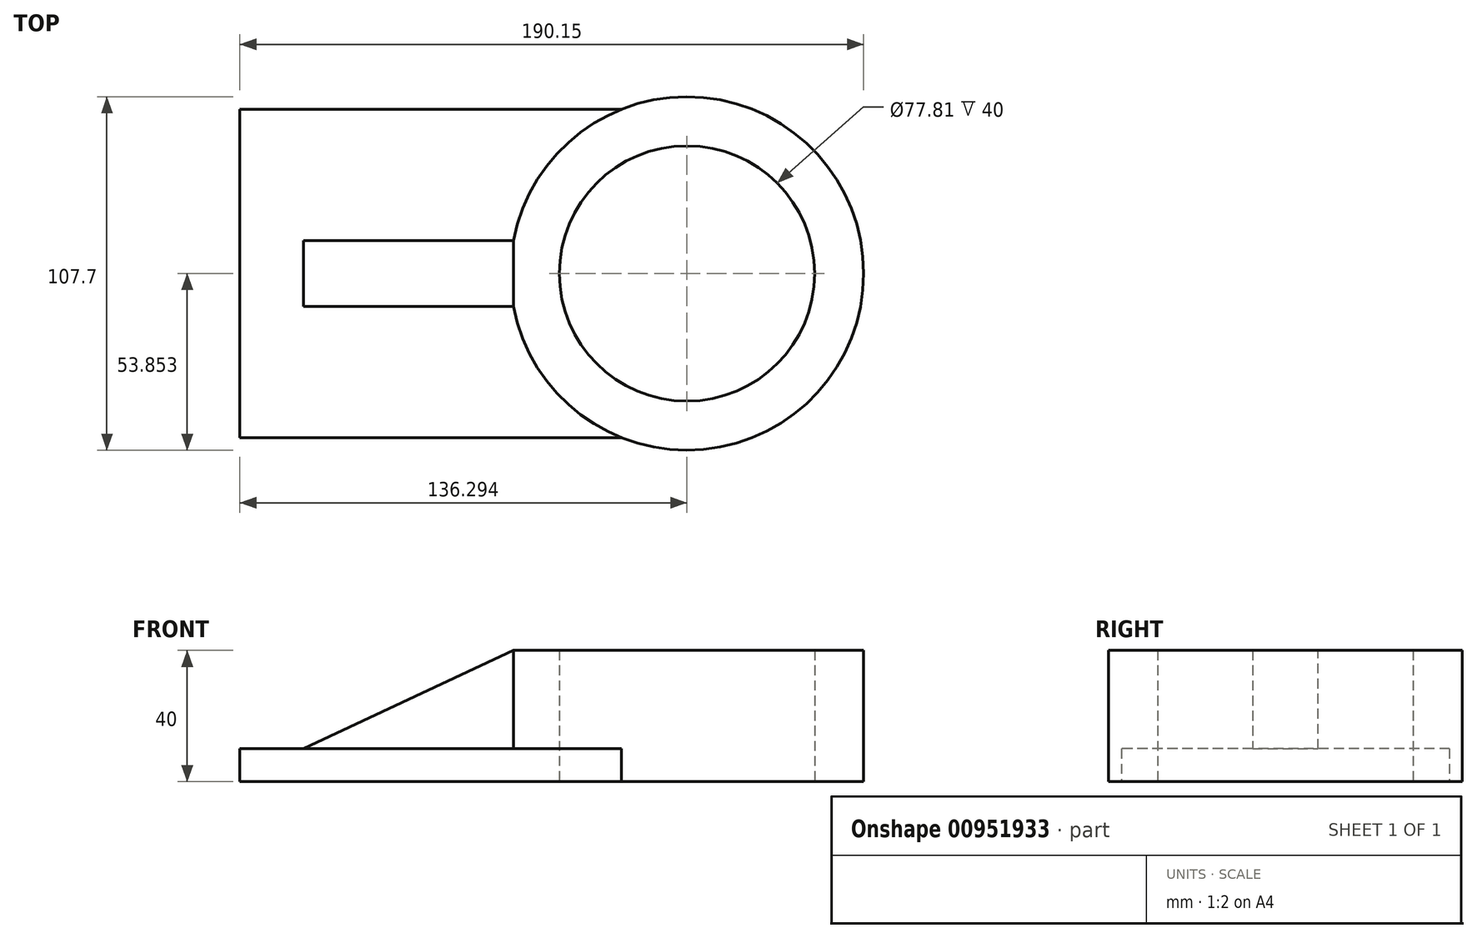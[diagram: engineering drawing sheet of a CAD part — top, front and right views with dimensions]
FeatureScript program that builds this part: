
annotation { "Feature Type Name" : "Feature", "Feature Type Description" : "" }
export const myFeature = defineFeature(function(context is Context, id is Id, definition is map)
    precondition{}
    {
        {
            var Q0;
            Q0=qCreatedBy(makeId("Top.planeOp"),FACE);
            var sketch = newSketch(context, id + "F0", { "sketchPlane" : qUnion([Q0])});
            skLineSegment(sketch, "E0.bottom", {"start": v(-44.41, 49.03) * mm, "end": v(71.88, 49.03) * mm});
            skLineSegment(sketch, "E0.top", {"start": v(-44.41, -50.97) * mm, "end": v(71.88, -50.97) * mm});
            skLineSegment(sketch, "E0.left", {"start": v(-44.41, 49.03) * mm, "end": v(-44.41, -50.97) * mm});
            skCircle(sketch, "E1", {"center": v(91.88, -0.97) * mm, "radius": 53.85 * mm});
            skCircle(sketch, "E2", {"center": v(91.88, -0.97) * mm, "radius": 38.9 * mm});
            skSolve(sketch);
        }
        {
            var Q0;
            Q0=makeQuery(id+"F0.imprint","IMPRINT",FACE,{"disambiguationData":[TD([[makeQuery(id+"F0.imprint","IMPRINT",EDGE,{"derivedFrom":sQuery(id+"F0.wireOp",EDGE,"E2")}),-1.0]])]});
            extrude(context, id + "F1", {"entities" : qUnion([Q0]), "depth" : 40 * mm, "offsetDistance" : 25 * mm});
        }
        {
            var Q0;
            {var subQ0=sQuery(id+"F0.wireOp",EDGE,"E0.bottom");Q0=makeQuery(id+"F0.imprint","IMPRINT",FACE,{"disambiguationData":[TD([[makeQuery(id+"F0.imprint","IMPRINT",EDGE,{"derivedFrom":subQ0}),-1.0]])]});}
            extrude(context, id + "F2", {"entities" : qUnion([Q0]), "operationType" : NewBodyOperationType.ADD, "depth" : 10 * mm, "offsetDistance" : 25 * mm});
        }
        {
            var Q0;
            Q0=makeQuery(id+"F2.opExtrude","CAP_FACE",FACE,{"disambiguationData":[OSD([sQuery(id+"F0.wireOp",EDGE,"E0.bottom"),sQuery(id+"F0.wireOp",EDGE,"E0.top"),sQuery(id+"F0.wireOp",EDGE,"E0.left"),sQuery(id+"F0.wireOp",EDGE,"E1")])],"isStart":false});
            var sketch = newSketch(context, id + "F3", { "sketchPlane" : qUnion([Q0])});
            skLineSegment(sketch, "E3", {"start": v(-44.41, 49.03) * mm, "end": v(-44.41, -0.97) * mm});
            skLineSegment(sketch, "E4", {"start": v(-24.97, -0.97) * mm, "end": v(-24.97, -10.97) * mm});
            skLineSegment(sketch, "E5", {"start": v(38.97, -10.97) * mm, "end": v(-24.97, -10.97) * mm});
            skLineSegment(sketch, "E6", {"start": v(-24.97, -0.97) * mm, "end": v(-24.97, 9.03) * mm});
            skLineSegment(sketch, "E7", {"start": v(-24.97, 9.03) * mm, "end": v(38.97, 9.03) * mm});
            skLineSegment(sketch, "E8", {"start": v(38.97, 9.03) * mm, "end": v(-24.97, 9.03) * mm});
            skSolve(sketch);
        }
        {
            var Q0;
            Q0=makeQuery(id+"F3.imprint","IMPRINT",FACE,{"disambiguationData":[TD([[makeQuery(id+"F3.imprint","IMPRINT",EDGE,{"derivedFrom":sQuery(id+"F3.wireOp",EDGE,"E4")}),1.0]])]});
            extrude(context, id + "F4", {"entities" : qUnion([Q0]), "operationType" : NewBodyOperationType.ADD, "depth" : 30 * mm, "offsetDistance" : 25 * mm});
        }
        {
            var Q0;
            Q0=makeQuery(id+"F4.opExtrude","SWEPT_FACE",FACE,{"disambiguationData":[OSD([sQuery(id+"F3.wireOp",EDGE,"E5")])]});
            var sketch = newSketch(context, id + "F5", { "sketchPlane" : qUnion([Q0])});
            skLineSegment(sketch, "E9", {"start": v(-24.97, 10) * mm, "end": v(38.97, 40) * mm});
            skSolve(sketch);
        }
        {
            var Q0;
            Q0 = qSketchRegion(id + "F5", true);
            var Q1;
            Q1=makeQuery(id+"F5.imprint","IMPRINT",FACE,{"disambiguationData":[TD([[makeQuery(id+"F5.imprint","IMPRINT",EDGE,{"derivedFrom":sQuery(id+"F5.wireOp",EDGE,"E9")}),1.0]])]});
            extrude(context, id + "F6", {"entities" : qUnion([Q0, Q1]), "operationType" : NewBodyOperationType.REMOVE, "oppositeDirection" : true, "depth" : 20 * mm, "offsetDistance" : 25 * mm});
        }
    });
